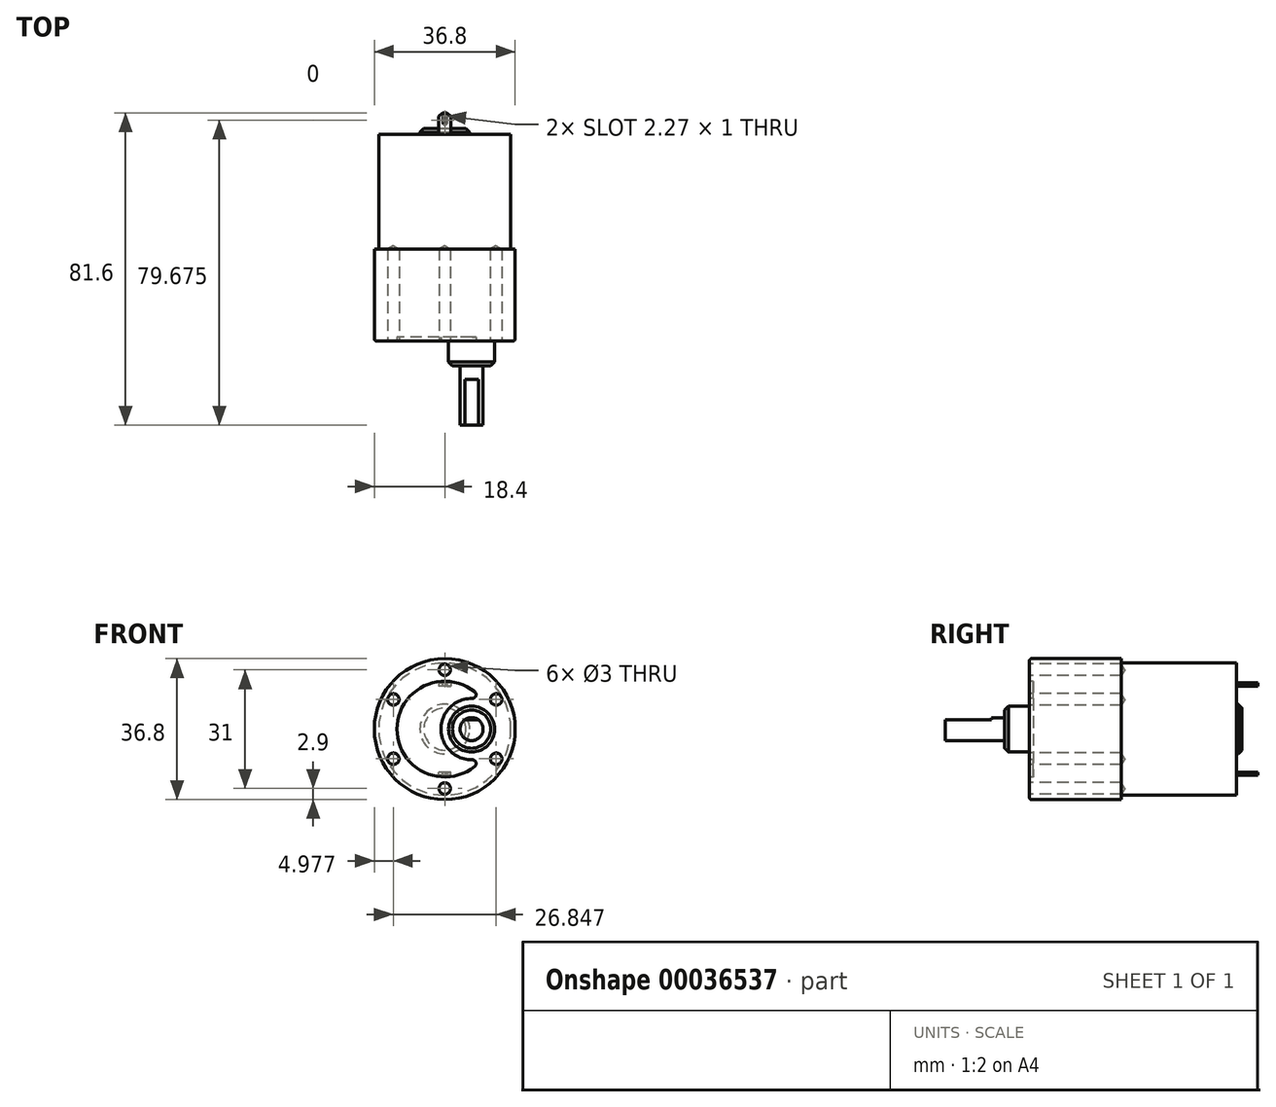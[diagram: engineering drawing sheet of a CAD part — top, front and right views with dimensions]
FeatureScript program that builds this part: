
annotation { "Feature Type Name" : "Feature", "Feature Type Description" : "" }
export const myFeature = defineFeature(function(context is Context, id is Id, definition is map)
    precondition{}
    {
        {
            var Q0;
            Q0=qCreatedBy(makeId("Front.planeOp"),FACE);
            var sketch = newSketch(context, id + "F0", { "sketchPlane" : qUnion([Q0])});
            skCircle(sketch, "E0", {"center": v(0, 0) * mm, "radius": 18.4 * mm});
            skSolve(sketch);
        }
        {
            var Q0;
            Q0 = qSketchRegion(id + "F0", true);
            extrude(context, id + "F1", {"entities" : qUnion([Q0]), "depth" : 24 * mm});
        }
        {
            var Q0;
            Q0=makeQuery(id+"F1.opExtrude","CAP_FACE",FACE,{"disambiguationData":[OSD([sQuery(id+"F0.wireOp",EDGE,"E0")])],"isStart":true});
            var sketch = newSketch(context, id + "F2", { "sketchPlane" : qUnion([Q0])});
            skCircle(sketch, "E1", {"center": v(0, 0) * mm, "radius": 17.25 * mm});
            skSolve(sketch);
        }
        {
            var Q0;
            Q0 = qSketchRegion(id + "F2", true);
            extrude(context, id + "F3", {"entities" : qUnion([Q0]), "operationType" : NewBodyOperationType.ADD, "depth" : 30 * mm});
        }
        {
            var Q0;
            Q0=makeQuery(id+"F1.opExtrude","CAP_FACE",FACE,{"disambiguationData":[OSD([sQuery(id+"F0.wireOp",EDGE,"E0")])],"isStart":false});
            var sketch = newSketch(context, id + "F4", { "sketchPlane" : qUnion([Q0])});
            skCircle(sketch, "E2", {"center": v(7, 0) * mm, "radius": 6 * mm});
            skSolve(sketch);
        }
        {
            var Q0;
            Q0 = qSketchRegion(id + "F4", true);
            extrude(context, id + "F5", {"entities" : qUnion([Q0]), "operationType" : NewBodyOperationType.ADD, "depth" : 6.5 * mm});
        }
        {
            var Q0;
            Q0=makeQuery(id+"F5.opExtrude","CAP_FACE",FACE,{"disambiguationData":[OSD([sQuery(id+"F4.wireOp",EDGE,"E2")])],"isStart":false});
            var sketch = newSketch(context, id + "F6", { "sketchPlane" : qUnion([Q0])});
            skCircle(sketch, "E3", {"center": v(7, 0) * mm, "radius": 3 * mm});
            skSolve(sketch);
        }
        {
            var Q0;
            Q0 = qSketchRegion(id + "F6", true);
            extrude(context, id + "F7", {"entities" : qUnion([Q0]), "operationType" : NewBodyOperationType.ADD, "depth" : 15.5 * mm});
        }
        {
            var Q0;
            Q0=makeQuery(id+"F5.opExtrude","CAP_EDGE",EDGE,{"disambiguationData":[OSD([sQuery(id+"F4.wireOp",EDGE,"E2")])],"isStart":false});
            chamfer(context, id + "F8", {"entities" : qUnion([Q0]), "width" : 1 * mm, "tangentPropagation" : true});
        }
        {
            var Q0;
            Q0=makeQuery(id+"F7.opExtrude","CAP_FACE",FACE,{"disambiguationData":[OSD([sQuery(id+"F6.wireOp",EDGE,"E3")])],"isStart":false});
            var sketch = newSketch(context, id + "F9", { "sketchPlane" : qUnion([Q0])});
            skLineSegment(sketch, "E4", {"start": v(5.2, 2.4) * mm, "end": v(8.8, 2.4) * mm});
            skArc(sketch, "E5", {"start": v(8.8, 2.4) * mm, "mid": v(7, 3) * mm, "end": v(5.2, 2.4) * mm});
            skSolve(sketch);
        }
        {
            var Q0;
            Q0=makeQuery(id+"F9.imprint","IMPRINT",FACE,{"disambiguationData":[TD([[makeQuery(id+"F9.imprint","IMPRINT",EDGE,{"derivedFrom":sQuery(id+"F9.wireOp",EDGE,"E4")}),1.0]])]});
            extrude(context, id + "F10", {"entities" : qUnion([Q0]), "operationType" : NewBodyOperationType.REMOVE, "oppositeDirection" : true, "depth" : 12 * mm});
        }
        {
            var Q0;
            Q0=makeQuery(id+"F1.opExtrude","CAP_FACE",FACE,{"disambiguationData":[OSD([sQuery(id+"F0.wireOp",EDGE,"E0")])],"isStart":false});
            var sketch = newSketch(context, id + "F11", { "sketchPlane" : qUnion([Q0])});
            skCircle(sketch, "E6", {"center": v(0, 15.5) * mm, "radius": 1.5 * mm});
            skCircle(sketch, "E7.1.0", {"center": v(-13.42, 7.75) * mm, "radius": 1.5 * mm});
            skCircle(sketch, "E7.2.0", {"center": v(-13.42, -7.75) * mm, "radius": 1.5 * mm});
            skCircle(sketch, "E7.3.0", {"center": v(0, -15.5) * mm, "radius": 1.5 * mm});
            skCircle(sketch, "E7.4.0", {"center": v(13.42, -7.75) * mm, "radius": 1.5 * mm});
            skCircle(sketch, "E7.5.0", {"center": v(13.42, 7.75) * mm, "radius": 1.5 * mm});
            skPoint(sketch, "E7.center", {"position": v(0, 0) * mm});
            skSolve(sketch);
        }
        {
            var Q0;
            Q0=sQuery(id+"F11.wireOp",VERTEX,"E6.center");
            var Q1;
            Q1=sQuery(id+"F11.wireOp",VERTEX,"E7.1.0.center");
            var Q2;
            Q2=sQuery(id+"F11.wireOp",VERTEX,"E7.2.0.center");
            var Q3;
            Q3=sQuery(id+"F11.wireOp",VERTEX,"E7.3.0.center");
            var Q4;
            Q4=sQuery(id+"F11.wireOp",VERTEX,"E7.4.0.center");
            var Q5;
            Q5=sQuery(id+"F11.wireOp",VERTEX,"E7.5.0.center");
            var Q6;
            Q6=makeQuery(id+"F1.opExtrude","SWEPT_BODY",BODY,{"disambiguationData":[OSD([sQuery(id+"F0.wireOp",EDGE,"E0")])]});
            hole(context, id + "F12", {"style" : HoleStyle.SIMPLE, "holeDiameter" : 3 * mm, "endStyle" : HoleEndStyle.BLIND, "holeDepth" : 24 * mm, "locations" : qUnion([Q0, Q1, Q2, Q3, Q4, Q5]), "scope" : qUnion([Q6])});
        }
        {
            var Q0;
            Q0=makeQuery(id+"F1.opExtrude","CAP_FACE",FACE,{"disambiguationData":[OSD([sQuery(id+"F0.wireOp",EDGE,"E0")])],"isStart":false});
            var sketch = newSketch(context, id + "F13", { "sketchPlane" : qUnion([Q0])});
            skArc(sketch, "E8", {"start": v(7.78, 9.78) * mm, "mid": v(-12.5, 0) * mm, "end": v(7.78, -9.78) * mm});
            skArc(sketch, "E9", {"start": v(7.14, 8) * mm, "mid": v(-1, 0) * mm, "end": v(7.14, -8) * mm});
            skPoint(sketch, "E10.visualSharp", {"position": v(10.09, 7.38) * mm});
            skArc(sketch, "E10.filletArc", {"start": v(7.14, 8) * mm, "mid": v(8.1, 8.66) * mm, "end": v(7.78, 9.78) * mm});
            skPoint(sketch, "E11.visualSharp", {"position": v(10.09, -7.38) * mm});
            skArc(sketch, "E11.filletArc", {"start": v(7.78, -9.78) * mm, "mid": v(8.1, -8.66) * mm, "end": v(7.14, -8) * mm});
            skSolve(sketch);
        }
        {
            var Q0;
            Q0=makeQuery(id+"F13.imprint","IMPRINT",FACE,{"disambiguationData":[TD([[makeQuery(id+"F13.imprint","IMPRINT",EDGE,{"derivedFrom":sQuery(id+"F13.wireOp",EDGE,"E8")}),1.0]])]});
            extrude(context, id + "F14", {"entities" : qUnion([Q0]), "operationType" : NewBodyOperationType.REMOVE, "oppositeDirection" : true, "depth" : 1 * mm});
        }
        {
            var Q0;
            Q0=makeQuery(id+"F3.opExtrude","CAP_FACE",FACE,{"disambiguationData":[OSD([sQuery(id+"F2.wireOp",EDGE,"E1")])],"isStart":false});
            var sketch = newSketch(context, id + "F15", { "sketchPlane" : qUnion([Q0])});
            skCircle(sketch, "E12", {"center": v(0, 0) * mm, "radius": 6.5 * mm});
            skSolve(sketch);
        }
        {
            var Q0;
            Q0=makeQuery(id+"F15.imprint","IMPRINT",FACE,{"disambiguationData":[TD([[makeQuery(id+"F15.imprint","IMPRINT",EDGE,{"derivedFrom":sQuery(id+"F15.wireOp",EDGE,"E12")}),1.0]])]});
            extrude(context, id + "F16", {"entities" : qUnion([Q0]), "operationType" : NewBodyOperationType.ADD, "depth" : 1.5 * mm});
        }
        {
            var Q0;
            Q0=makeQuery(id+"F16.opExtrude","CAP_EDGE",EDGE,{"disambiguationData":[OSD([sQuery(id+"F15.wireOp",EDGE,"E12")])],"isStart":false});
            chamfer(context, id + "F17", {"entities" : qUnion([Q0]), "width" : 1 * mm, "tangentPropagation" : true});
        }
        {
            var Q0;
            Q0=makeQuery(id+"F3.opExtrude","CAP_FACE",FACE,{"disambiguationData":[OSD([sQuery(id+"F2.wireOp",EDGE,"E1")])],"isStart":false});
            var sketch = newSketch(context, id + "F18", { "sketchPlane" : qUnion([Q0])});
            skLineSegment(sketch, "E13.bottom", {"start": v(-1.59, 12.05) * mm, "end": v(1.59, 12.05) * mm});
            skLineSegment(sketch, "E13.top", {"start": v(-1.59, 11.26) * mm, "end": v(1.59, 11.26) * mm});
            skLineSegment(sketch, "E13.left", {"start": v(-1.59, 12.05) * mm, "end": v(-1.59, 11.26) * mm});
            skLineSegment(sketch, "E13.right", {"start": v(1.59, 12.05) * mm, "end": v(1.59, 11.26) * mm});
            skLineSegment(sketch, "E14", {"start": v(0, 0) * mm, "end": v(0, 12.05) * mm, "construction": true});
            skLineSegment(sketch, "E15", {"start": v(0, 0) * mm, "end": v(8.8, 0) * mm, "construction": true});
            skLineSegment(sketch, "E16.MirrorCS", {"start": v(-1.59, -12.05) * mm, "end": v(1.59, -12.05) * mm});
            skLineSegment(sketch, "E17.MirrorCS", {"start": v(-1.59, -12.05) * mm, "end": v(-1.59, -11.26) * mm});
            skLineSegment(sketch, "E18.MirrorCS", {"start": v(-1.59, -11.26) * mm, "end": v(1.59, -11.26) * mm});
            skLineSegment(sketch, "E19.MirrorCS", {"start": v(1.59, -12.05) * mm, "end": v(1.59, -11.26) * mm});
            skSolve(sketch);
        }
        {
            var Q0;
            Q0=makeQuery(id+"F18.imprint","IMPRINT",FACE,{"disambiguationData":[TD([[makeQuery(id+"F18.imprint","IMPRINT",EDGE,{"derivedFrom":sQuery(id+"F18.wireOp",EDGE,"E13.bottom")}),-1.0]])]});
            var Q1;
            Q1=makeQuery(id+"F18.imprint","IMPRINT",FACE,{"disambiguationData":[TD([[makeQuery(id+"F18.imprint","IMPRINT",EDGE,{"derivedFrom":sQuery(id+"F18.wireOp",EDGE,"E16.MirrorCS")}),1.0]])]});
            extrude(context, id + "F19", {"entities" : qUnion([Q0, Q1]), "operationType" : NewBodyOperationType.ADD, "depth" : 5.6 * mm});
        }
        {
            var Q0;
            Q0=makeQuery(id+"F19.opExtrude","CAP_EDGE",EDGE,{"disambiguationData":[OSD([sQuery(id+"F18.wireOp",EDGE,"E13.right")])],"isStart":false});
            var Q1;
            Q1=makeQuery(id+"F19.opExtrude","CAP_EDGE",EDGE,{"disambiguationData":[OSD([sQuery(id+"F18.wireOp",EDGE,"E13.left")])],"isStart":false});
            var Q2;
            Q2=makeQuery(id+"F19.opExtrude","CAP_EDGE",EDGE,{"disambiguationData":[OSD([sQuery(id+"F18.wireOp",EDGE,"E17.MirrorCS")])],"isStart":false});
            var Q3;
            Q3=makeQuery(id+"F19.opExtrude","CAP_EDGE",EDGE,{"disambiguationData":[OSD([sQuery(id+"F18.wireOp",EDGE,"E19.MirrorCS")])],"isStart":false});
            chamfer(context, id + "F20", {"entities" : qUnion([Q0, Q1, Q2, Q3]), "width" : 1 * mm, "tangentPropagation" : true});
        }
        {
            var Q0;
            Q0=makeQuery(id+"F19.opExtrude","SWEPT_FACE",FACE,{"disambiguationData":[OSD([sQuery(id+"F18.wireOp",EDGE,"E13.bottom")])]});
            var sketch = newSketch(context, id + "F21", { "sketchPlane" : qUnion([Q0])});
            skArc(sketch, "E20", {"start": v(0.5, 34.31) * mm, "mid": v(0, 34.81) * mm, "end": v(-0.5, 34.31) * mm});
            skArc(sketch, "E21", {"start": v(-0.5, 33.04) * mm, "mid": v(0, 32.54) * mm, "end": v(0.5, 33.04) * mm});
            skLineSegment(sketch, "E22", {"start": v(-0.5, 34.31) * mm, "end": v(-0.5, 33.04) * mm});
            skLineSegment(sketch, "E23", {"start": v(0.5, 34.31) * mm, "end": v(0.5, 33.04) * mm});
            skSolve(sketch);
        }
        {
            var Q0;
            Q0 = qSketchRegion(id + "F21", true);
            extrude(context, id + "F22", {"entities" : qUnion([Q0]), "operationType" : NewBodyOperationType.REMOVE, "oppositeDirection" : true, "depth" : 25.4 * mm});
        }
        {
            var Q0;
            Q0=makeQuery(id+"F1.opExtrude","CAP_EDGE",EDGE,{"disambiguationData":[OSD([sQuery(id+"F0.wireOp",EDGE,"E0")])],"isStart":false});
            fillet(context, id + "F23", {"entities" : qUnion([Q0]), "radius" : .5 * mm, "tangentPropagation" : true, "allowEdgeOverflow" : false});
        }
    });
